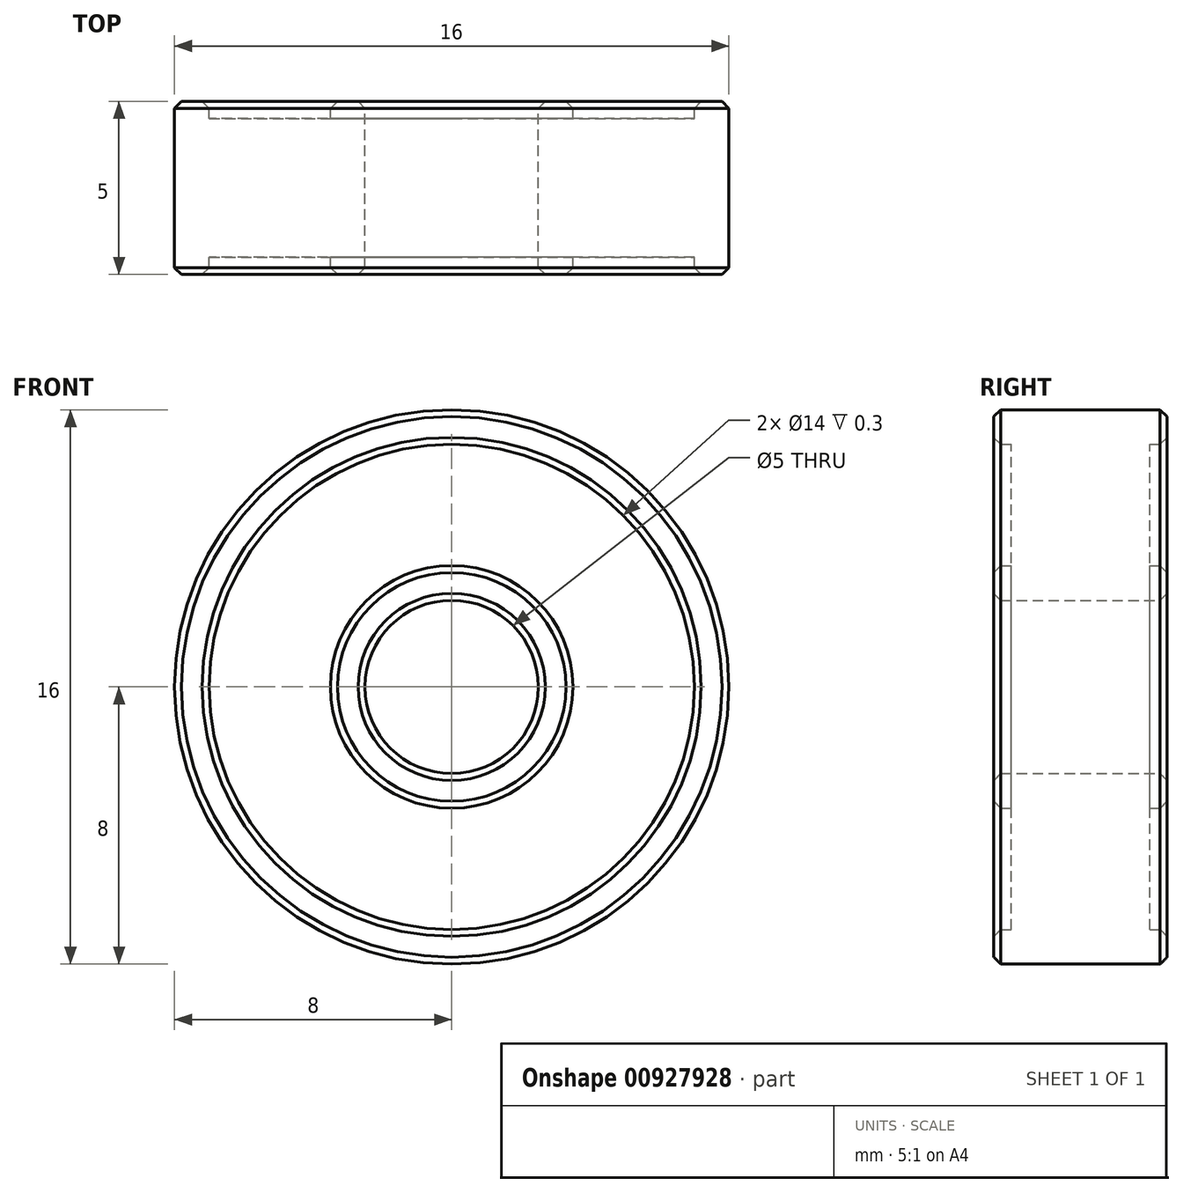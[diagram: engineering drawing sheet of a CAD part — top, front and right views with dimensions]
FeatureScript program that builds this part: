
annotation { "Feature Type Name" : "Feature", "Feature Type Description" : "" }
export const myFeature = defineFeature(function(context is Context, id is Id, definition is map)
    precondition{}
    {
        {
            var Q0;
            Q0=qCreatedBy(makeId("Front.planeOp"),FACE);
            var sketch = newSketch(context, id + "F0", { "sketchPlane" : qUnion([Q0])});
            skCircle(sketch, "E0", {"center": v(0, 0) * mm, "radius": 8 * mm});
            skCircle(sketch, "E1", {"center": v(0, 0) * mm, "radius": 7 * mm});
            skCircle(sketch, "E2", {"center": v(0, 0) * mm, "radius": 3.5 * mm});
            skCircle(sketch, "E3", {"center": v(0, 0) * mm, "radius": 2.5 * mm});
            skSolve(sketch);
        }
        {
            var Q0;
            Q0=makeQuery(id+"F0.imprint","IMPRINT",FACE,{"disambiguationData":[TD([[makeQuery(id+"F0.imprint","IMPRINT",EDGE,{"derivedFrom":sQuery(id+"F0.wireOp",EDGE,"E0")}),1.0]])]});
            var Q1;
            Q1=makeQuery(id+"F0.imprint","IMPRINT",FACE,{"disambiguationData":[TD([[makeQuery(id+"F0.imprint","IMPRINT",EDGE,{"derivedFrom":sQuery(id+"F0.wireOp",EDGE,"E2")}),1.0]])]});
            extrude(context, id + "F1", {"entities" : qUnion([Q0, Q1]), "endBound" : BoundingType.SYMMETRIC, "offsetDistance" : 25 * mm, "depth" : 5 * mm});
        }
        {
            var Q0;
            Q0=makeQuery(id+"F0.imprint","IMPRINT",FACE,{"disambiguationData":[TD([[makeQuery(id+"F0.imprint","IMPRINT",EDGE,{"derivedFrom":sQuery(id+"F0.wireOp",EDGE,"E1")}),1.0]])]});
            extrude(context, id + "F2", {"entities" : qUnion([Q0]), "operationType" : NewBodyOperationType.ADD, "endBound" : BoundingType.SYMMETRIC, "offsetDistance" : 25 * mm, "depth" : 4 * mm});
        }
        {
            var Q0;
            Q0=makeQuery(id+"F1.opExtrude","CAP_FACE",FACE,{"disambiguationData":[OSD([sQuery(id+"F0.wireOp",EDGE,"E0"),sQuery(id+"F0.wireOp",EDGE,"E1")])],"isStart":false});
            var Q1;
            Q1=makeQuery(id+"F1.opExtrude","CAP_FACE",FACE,{"disambiguationData":[OSD([sQuery(id+"F0.wireOp",EDGE,"E2"),sQuery(id+"F0.wireOp",EDGE,"E3")])],"isStart":false});
            var Q2;
            Q2=makeQuery(id+"F1.opExtrude","CAP_FACE",FACE,{"disambiguationData":[OSD([sQuery(id+"F0.wireOp",EDGE,"E0"),sQuery(id+"F0.wireOp",EDGE,"E1")])],"isStart":true});
            var Q3;
            Q3=makeQuery(id+"F1.opExtrude","CAP_FACE",FACE,{"disambiguationData":[OSD([sQuery(id+"F0.wireOp",EDGE,"E2"),sQuery(id+"F0.wireOp",EDGE,"E3")])],"isStart":true});
            chamfer(context, id + "F3", {"entities" : qUnion([Q0, Q1, Q2, Q3]), "width" : .2 * mm, "tangentPropagation" : true});
        }
    });
